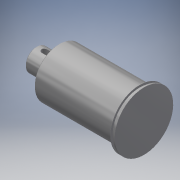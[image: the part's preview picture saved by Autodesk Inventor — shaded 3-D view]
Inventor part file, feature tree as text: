
AUTODESK INVENTOR PART (.ipt)
format: ipt  version: 2019 (Build 230136000, 136)  size: 180,224 bytes
history: native  units: mm
features: other x8, chamfer x2, fillet x1
ambient origin geometry x6: Origin, XZ Plane, XY Plane, X Axis, Y Axis, Z Axis
bodies: Body1 (feature_tree)
feature tree (11):
  other  "實體1"
  other  "迴轉1"
  chamfer  "倒角1"  [1 undecoded]
  fillet  "圓角1"  Radius=10.0mm
  other  "鍵槽1"
  chamfer  "倒角2"  Distance=22.0mm
  other  "扣環槽1"
  other  "起始平面"
  other  "主要草圖"
  other  "iFeature3:1"
  other  "iFeature27:1"
note: 1 required parameter value undecoded (feature->parameter linkage not recoverable at this tier; creation-order binding heuristic only, values carry confidence <= 0.55)
